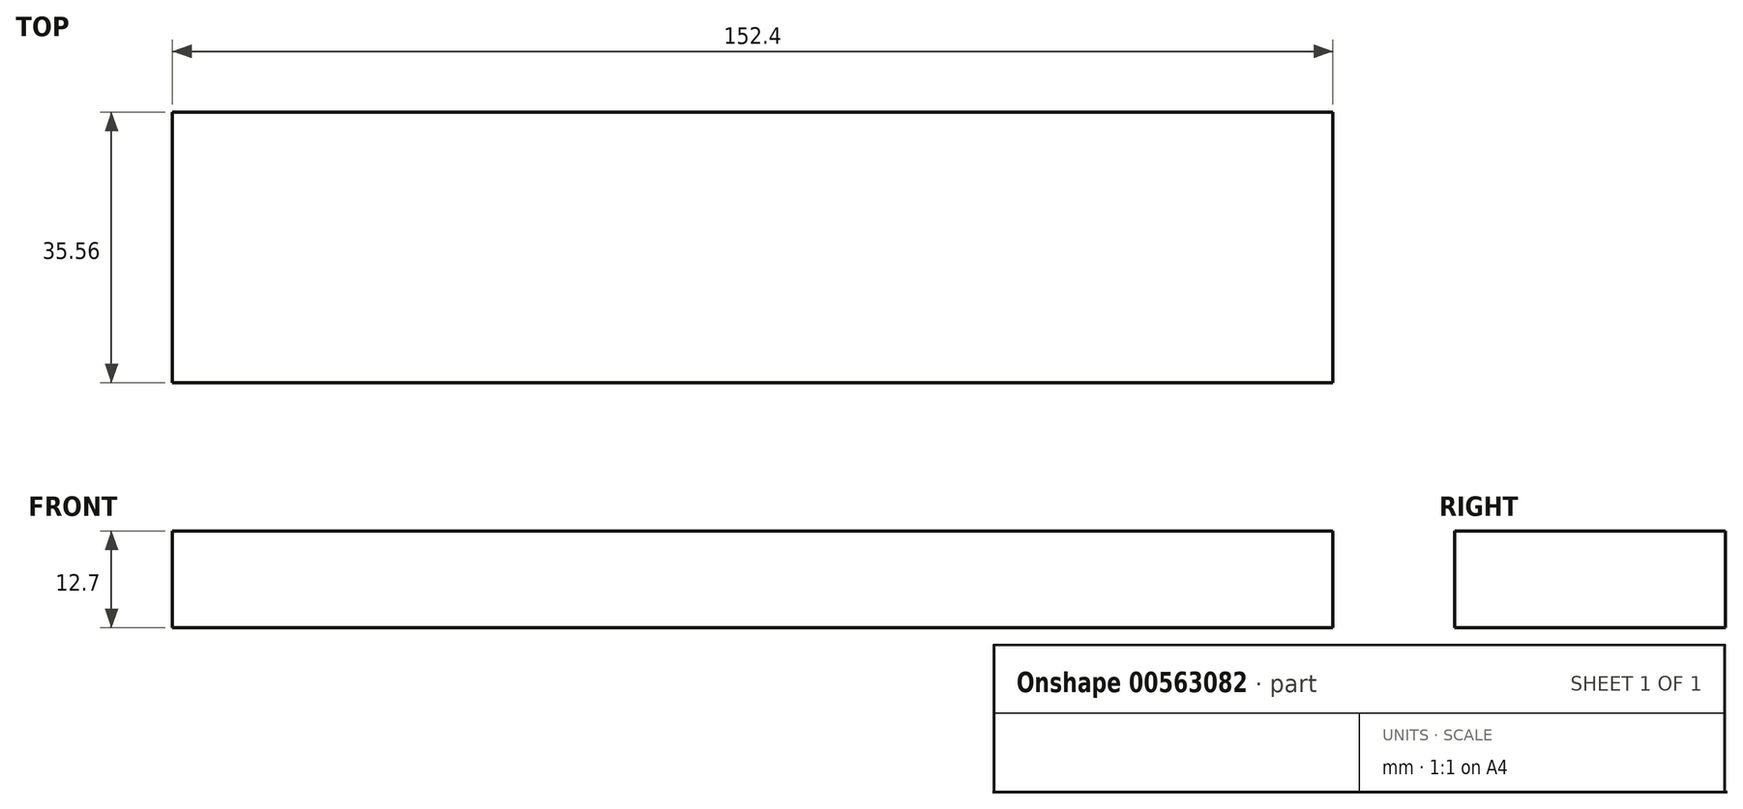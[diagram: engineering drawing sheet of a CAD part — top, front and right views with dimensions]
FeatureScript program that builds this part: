
annotation { "Feature Type Name" : "Feature", "Feature Type Description" : "" }
export const myFeature = defineFeature(function(context is Context, id is Id, definition is map)
    precondition{}
    {
        {
            var Q0;
            Q0=qCreatedBy(makeId("Top.planeOp"),FACE);
            var sketch = newSketch(context, id + "F0", { "sketchPlane" : qUnion([Q0])});
            skLineSegment(sketch, "E0.bottom", {"start": v(-24.42, 17.65) * mm, "end": v(127.98, 17.65) * mm});
            skLineSegment(sketch, "E0.top", {"start": v(-24.42, -17.9) * mm, "end": v(127.98, -17.9) * mm});
            skLineSegment(sketch, "E0.left", {"start": v(-24.42, 17.65) * mm, "end": v(-24.42, -17.9) * mm});
            skLineSegment(sketch, "E0.right", {"start": v(127.98, 17.65) * mm, "end": v(127.98, -17.9) * mm});
            skSolve(sketch);
        }
        {
            var Q0;
            Q0 = qSketchRegion(id + "F0", true);
            extrude(context, id + "F1", {"entities" : qUnion([Q0]), "depth" : 12.7 * mm, "offsetDistance" : 25.4 * mm});
        }
    });
